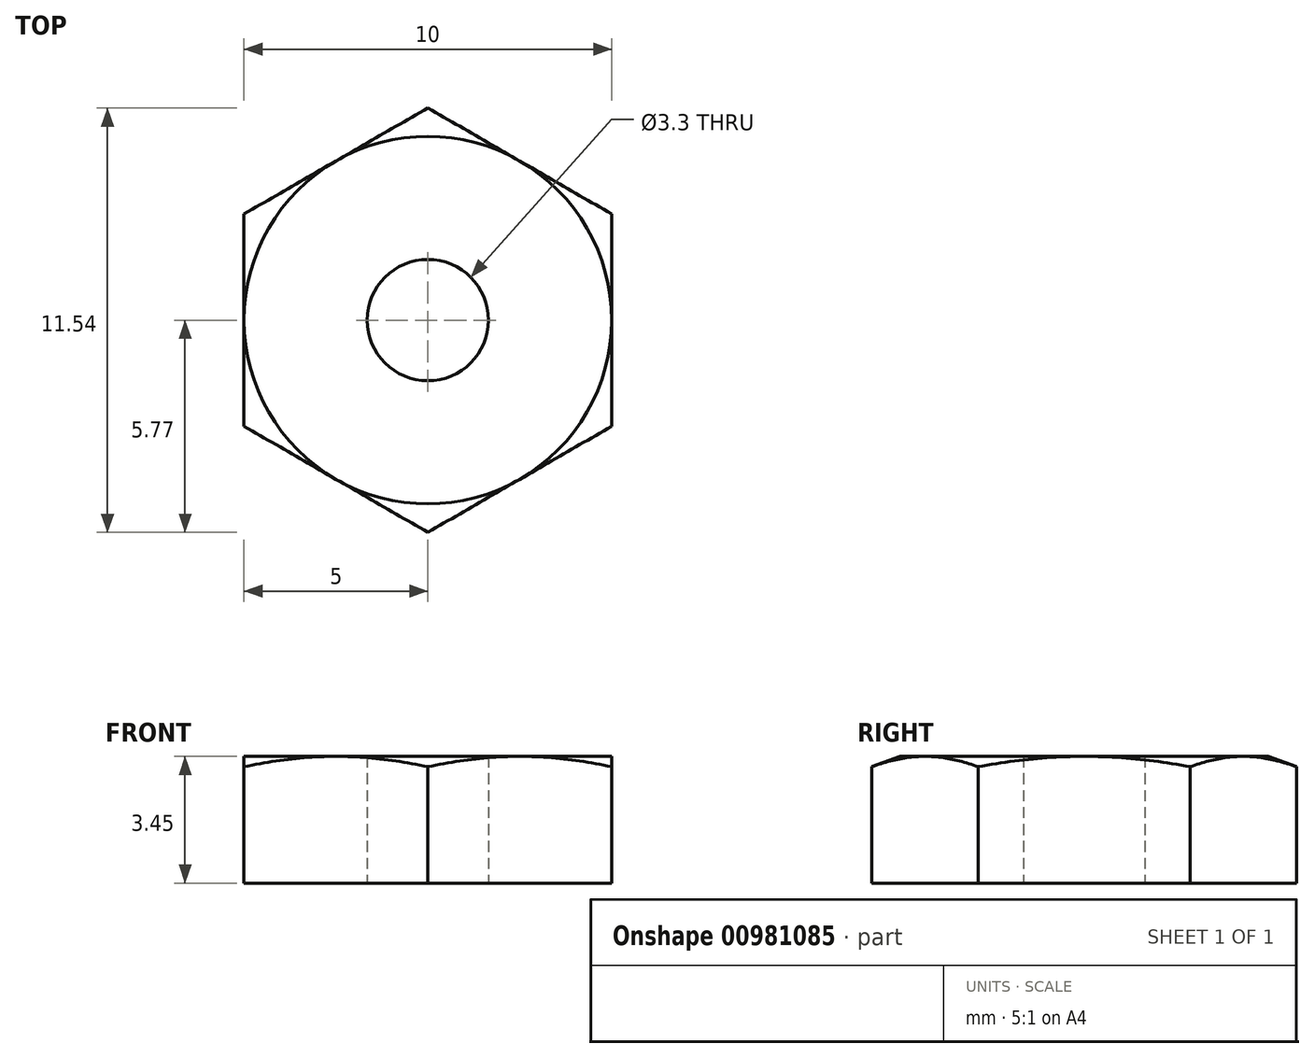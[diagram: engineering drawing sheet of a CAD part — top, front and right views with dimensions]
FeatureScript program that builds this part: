
annotation { "Feature Type Name" : "Feature", "Feature Type Description" : "" }
export const myFeature = defineFeature(function(context is Context, id is Id, definition is map)
    precondition{}
    {
        {
            var Q0;
            Q0=qCreatedBy(makeId("Top.planeOp"),FACE);
            var sketch = newSketch(context, id + "F0", { "sketchPlane" : qUnion([Q0])});
            skCircle(sketch, "E0.cCircle", {"center": v(0, 0) * mm, "radius": 5 * mm, "construction": true});
            skLineSegment(sketch, "E0.0", {"start": v(5, 2.89) * mm, "end": v(5, -2.89) * mm});
            skLineSegment(sketch, "E0.1", {"start": v(5, -2.89) * mm, "end": v(0, -5.77) * mm});
            skLineSegment(sketch, "E0.2", {"start": v(0, -5.77) * mm, "end": v(-5, -2.89) * mm});
            skLineSegment(sketch, "E0.3", {"start": v(-5, -2.89) * mm, "end": v(-5, 2.89) * mm});
            skLineSegment(sketch, "E0.4", {"start": v(-5, 2.89) * mm, "end": v(0, 5.77) * mm});
            skLineSegment(sketch, "E0.5", {"start": v(0, 5.77) * mm, "end": v(5, 2.89) * mm});
            skPoint(sketch, "E0.0.midPoint", {"position": v(5, 0) * mm});
            skSolve(sketch);
        }
        {
            var Q0;
            Q0 = qSketchRegion(id + "F0", true);
            extrude(context, id + "F1", {"entities" : qUnion([Q0]), "depth" : 3.45 * mm, "offsetDistance" : 25 * mm});
        }
        {
            var Q0;
            Q0=qCreatedBy(makeId("Front.planeOp"),FACE);
            var sketch = newSketch(context, id + "F2", { "sketchPlane" : qUnion([Q0])});
            skLineSegment(sketch, "E1", {"start": v(0, 0) * mm, "end": v(0, 3.45) * mm, "construction": true});
            skLineSegment(sketch, "E2", {"start": v(5, 3.45) * mm, "end": v(6.92, 3.45) * mm});
            skLineSegment(sketch, "E3", {"start": v(6.92, 3.45) * mm, "end": v(6.92, 2.75) * mm});
            skLineSegment(sketch, "E4", {"start": v(6.92, 2.75) * mm, "end": v(5, 3.45) * mm});
            skSolve(sketch);
        }
        {
            var Q0;
            Q0 = qSketchRegion(id + "F2", true);
            var Q1;
            Q1=sQuery(id+"F2.wireOp",EDGE,"E1");
            revolve(context, id + "F3", {"operationType" : NewBodyOperationType.REMOVE, "surfaceOperationType" : NewSurfaceOperationType.NEW, "entities" : qUnion([Q0]), "axis" : qUnion([Q1]), "revolveType" : RevolveType.FULL, "oppositeDirection" : true});
        }
        {
            var Q0;
            Q0=makeQuery(id+"F1.opExtrude","CAP_FACE",FACE,{"disambiguationData":[OSD([sQuery(id+"F0.wireOp",EDGE,"E0.0"),sQuery(id+"F0.wireOp",EDGE,"E0.1"),sQuery(id+"F0.wireOp",EDGE,"E0.2"),sQuery(id+"F0.wireOp",EDGE,"E0.3"),sQuery(id+"F0.wireOp",EDGE,"E0.4"),sQuery(id+"F0.wireOp",EDGE,"E0.5")])],"isStart":false});
            var sketch = newSketch(context, id + "F4", { "sketchPlane" : qUnion([Q0])});
            skPoint(sketch, "E5", {"position": v(0, 0) * mm});
            skSolve(sketch);
        }
        {
            var Q0;
            Q0=sQuery(id+"F4.wireOp",VERTEX,"E5");
            var Q1;
            Q1=makeQuery(id+"F1.opExtrude","SWEPT_BODY",BODY,{"disambiguationData":[OSD([sQuery(id+"F0.wireOp",EDGE,"E0.0"),sQuery(id+"F0.wireOp",EDGE,"E0.1"),sQuery(id+"F0.wireOp",EDGE,"E0.2"),sQuery(id+"F0.wireOp",EDGE,"E0.3"),sQuery(id+"F0.wireOp",EDGE,"E0.4"),sQuery(id+"F0.wireOp",EDGE,"E0.5")])]});
            hole(context, id + "F5", {"style" : HoleStyle.SIMPLE, "endStyle" : HoleEndStyle.THROUGH, "standardTappedOrClearance" : lookupTablePath({ "standard" : "ISO", "engagement" : "75%", "pitch" : "0.7 mm", "size" : "M4", "type" : "Tapped" }), "standardBlindInLast" : lookupTablePath({ "standard" : "ISO", "fit" : "Normal", "engagement" : "75%", "pitch" : "0.7 mm", "size" : "M4", "type" : "Clearance & tapped" }), "holeDiameter" : 3.3 * mm, "majorDiameter" : 4 * mm, "showTappedDepth" : true, "isTappedThrough" : true, "tappedDepth" : 12 * mm, "tapClearance" : 3, "startFromSketch" : true, "locations" : qUnion([Q0]), "scope" : qUnion([Q1])});
        }
    });
